# Revit family: НЕВАТОМ_Секция бактерицидная SUB_20220407
name_source: partatom
category: Арматура воздуховодов
revit_build: Autodesk Revit 2017 (Build: 20170118_1100(x64)
units: mm (PartAtom-declared; Revit-internal decimal feet)

## family parameters
Всегда вертикально = Нет
На основе рабочей плоскости = Нет
Общий = Нет
При загрузке вырезать с полостями = Нет
Размер круглого соединителя = Использовать диаметр
Тип детали = Вставляется

## types (48) — shared parameters
ADSK_Завод-изготовитель = NEVATOM
ADSK_Материал наименование = Оцинкованная сталь
ADSK_Наименование = Секции ультрафиолетовой бактерицидной обработки (SUB)
ADSK_Напряжение = 230 В
ADSK_Потеря давления воздуха = 0.0 Па
ADSK_Размер_Ширина = 1440 мм
ADSK_Ток = 0 А
L = 1440 мм
Nevatom_URL = https://t.me
t = 2 мм
Материал корпуса = Материал корпуса
Толщина крышки = 50 мм

## per-type parameters (varying)
| type | A | ADSK_Единица измерения | ADSK_Марка | ADSK_Масса | ADSK_Масса_Текст | ADSK_Полная мощность | ADSK_Размер_Высота | ADSK_Размер_Длина | ADSK_Расход воздуха | B | C | D | E | F | M |
| SUB-400х200-2 | 400 мм | шт. | 400х200-2 | 17 | 17.0 кг | 0 кВт | 250 мм | 450 мм | 1152.0 м³/ч | 200 мм | 450 мм | 250 мм | 423 мм | 223 мм | 9 мм |
| SUB-400х200-4 | 400 мм | шт. | 400х200-4 | 20 | 20.0 кг | 0 кВт | 250 мм | 450 мм | 1152.0 м³/ч | 200 мм | 450 мм | 250 мм | 423 мм | 223 мм | 9 мм |
| SUB-400х200-6 | 400 мм | шт. | 400х200-6 | 22 | 22.0 кг | 0 кВт | 250 мм | 450 мм | 1152.0 м³/ч | 200 мм | 450 мм | 250 мм | 423 мм | 223 мм | 9 мм |
| SUB-400х200-8 | 400 мм | шт. | 400х200-8 | 25 | 25.0 кг | 1 кВт | 250 мм | 450 мм | 1152.0 м³/ч | 200 мм | 450 мм | 250 мм | 423 мм | 223 мм | 9 мм |
| SUB-500х250-2 | 500 мм | шт. | 500х250-2 | 21 | 21.0 кг | 0 кВт | 300 мм | 550 мм | 1800.0 м³/ч | 250 мм | 550 мм | 300 мм | 523 мм | 273 мм | 9 мм |
| SUB-500х250-4 | 500 мм | шт. | 500х250-4 | 23 | 23.0 кг | 0 кВт | 300 мм | 550 мм | 1800.0 м³/ч | 250 мм | 550 мм | 300 мм | 523 мм | 273 мм | 9 мм |
| SUB-500х250-6 | 500 мм | шт. | 500х250-6 | 25 | 25.0 кг | 0 кВт | 300 мм | 550 мм | 1800.0 м³/ч | 250 мм | 550 мм | 300 мм | 523 мм | 273 мм | 9 мм |
| SUB-500х250-8 | 500 мм | шт. | 500х250-8 | 28 | 28.0 кг | 1 кВт | 300 мм | 550 мм | 1800.0 м³/ч | 250 мм | 550 мм | 300 мм | 523 мм | 273 мм | 9 мм |
| SUB-500х250-10 | 500 мм | шт. | 500х250-10 | 30 | 30.0 кг | 1 кВт | 300 мм | 550 мм | 1800.0 м³/ч | 250 мм | 550 мм | 300 мм | 523 мм | 273 мм | 9 мм |
| SUB-500х250-12 | 500 мм | шт. | 500х250-12 | 33 | 33.0 кг | 1 кВт | 300 мм | 550 мм | 1800.0 м³/ч | 250 мм | 550 мм | 300 мм | 523 мм | 273 мм | 9 мм |
| SUB-500х300-4 | 500 мм | шт. | 500х300-4 | 24 | 24.0 кг | 0 кВт | 350 мм | 550 мм | 2150.0 м³/ч | 300 мм | 550 мм | 350 мм | 523 мм | 323 мм | 9 мм |
| SUB-500х300-6 | 500 мм | шт. | 500х300-6 | 27 | 27.0 кг | 0 кВт | 350 мм | 550 мм | 2150.0 м³/ч | 300 мм | 550 мм | 350 мм | 523 мм | 323 мм | 9 мм |
| SUB-500х300-8 | 500 мм | шт. | 500х300-8 | 29 | 29.0 кг | 1 кВт | 350 мм | 550 мм | 2150.0 м³/ч | 300 мм | 550 мм | 350 мм | 523 мм | 323 мм | 9 мм |
| SUB-500х300-10 | 500 мм | шт. | 500х300-10 | 31 | 31.0 кг | 1 кВт | 350 мм | 550 мм | 2150.0 м³/ч | 300 мм | 550 мм | 350 мм | 523 мм | 323 мм | 9 мм |
| SUB-500х300-12 | 500 мм | шт. | 500х300-12 | 34 | 34.0 кг | 1 кВт | 350 мм | 550 мм | 2150.0 м³/ч | 300 мм | 550 мм | 350 мм | 523 мм | 323 мм | 9 мм |
| SUB-600х300-4 | 600 мм | шт. | 600х300-4 | 28 | 28.0 кг | 0 кВт | 350 мм | 650 мм | 2600.0 м³/ч | 300 мм | 650 мм | 350 мм | 623 мм | 323 мм | 9 мм |
| SUB-600х300-6 | 600 мм | шт. | 600х300-6 | 29 | 29.0 кг | 0 кВт | 350 мм | 650 мм | 2600.0 м³/ч | 300 мм | 650 мм | 350 мм | 623 мм | 323 мм | 9 мм |
| SUB-600х300-8 | 600 мм | шт. | 600х300-8 | 30 | 30.0 кг | 1 кВт | 350 мм | 650 мм | 2600.0 м³/ч | 300 мм | 650 мм | 350 мм | 623 мм | 323 мм | 9 мм |
| SUB-600х300-10 | 600 мм | шт. | 600х300-10 | 31 | 31.0 кг | 1 кВт | 350 мм | 650 мм | 2600.0 м³/ч | 300 мм | 650 мм | 350 мм | 623 мм | 323 мм | 9 мм |
| SUB-600х300-12 | 600 мм | шт. | 600х300-12 | 32 | 32.0 кг | 1 кВт | 350 мм | 650 мм | 2600.0 м³/ч | 300 мм | 650 мм | 350 мм | 623 мм | 323 мм | 9 мм |
| SUB-600х300-14 | 600 мм | шт. | 600х300-14 | 33 | 33.0 кг | 1 кВт | 350 мм | 650 мм | 2600.0 м³/ч | 300 мм | 650 мм | 350 мм | 623 мм | 323 мм | 9 мм |
| SUB-600х350-4 | 600 мм | шт. | 600х350-4 | 29 | 29.0 кг | 0 кВт | 400 мм | 650 мм | 3000.0 м³/ч | 350 мм | 650 мм | 400 мм | 623 мм | 373 мм | 9 мм |
| SUB-600х350-6 | 600 мм | 31.0 шт. | 600х350-6 | 31 | кг | 0 кВт | 400 мм | 650 мм | 3000.0 м³/ч | 350 мм | 650 мм | 400 мм | 623 мм | 373 мм | 9 мм |
| SUB-600х350-8 | 600 мм | шт. | 600х350-8 | 33 | 33.0 кг | 1 кВт | 400 мм | 650 мм | 3000.0 м³/ч | 350 мм | 650 мм | 400 мм | 623 мм | 373 мм | 9 мм |
| SUB-600х350-10 | 600 мм | шт. | 600х350-10 | 36 | 36.0 кг | 1 кВт | 400 мм | 650 мм | 3000.0 м³/ч | 350 мм | 650 мм | 400 мм | 623 мм | 373 мм | 9 мм |
| SUB-600х350-12 | 600 мм | шт. | 600х350-12 | 39 | 39.0 кг | 1 кВт | 400 мм | 650 мм | 3000.0 м³/ч | 350 мм | 650 мм | 400 мм | 623 мм | 373 мм | 9 мм |
| SUB-600х350-14 | 600 мм | шт. | 600х350-14 | 41 | 41.0 кг | 1 кВт | 400 мм | 650 мм | 3000.0 м³/ч | 350 мм | 650 мм | 400 мм | 623 мм | 373 мм | 9 мм |
| SUB-700х400-6 | 700 мм | шт. | 700х400-6 | 34 | 34.0 кг | 0 кВт | 457 мм | 757 мм | 4000.0 м³/ч | 400 мм | 757 мм | 457 мм | 727 мм | 427 мм | 11 мм |
| SUB-700х400-10 | 700 мм | шт. | 700х400-10 | 39 | 39.0 кг | 1 кВт | 457 мм | 757 мм | 4000.0 м³/ч | 400 мм | 757 мм | 457 мм | 727 мм | 427 мм | 11 мм |
| SUB-700х400-12 | 700 мм | шт. | 700х400-12 | 41 | 41.0 кг | 1 кВт | 457 мм | 757 мм | 4000.0 м³/ч | 400 мм | 757 мм | 457 мм | 727 мм | 427 мм | 11 мм |
| SUB-700х400-14 | 700 мм | шт. | 700х400-14 | 44 | 44.0 кг | 1 кВт | 457 мм | 757 мм | 4000.0 м³/ч | 400 мм | 757 мм | 457 мм | 727 мм | 427 мм | 11 мм |
| SUB-700х400-18 | 700 мм | шт. | 700х400-18 | 48 | 48.0 кг | 1 кВт | 457 мм | 757 мм | 4000.0 м³/ч | 400 мм | 757 мм | 457 мм | 727 мм | 427 мм | 11 мм |
| SUB-800х500-8 | 800 мм | шт. | 800х500-8 | 41 | 41.0 кг | 1 кВт | 557 мм | 857 мм | 5700.0 м³/ч | 500 мм | 857 мм | 557 мм | 827 мм | 527 мм | 11 мм |
| SUB-800х500-10 | 800 мм | шт. | 800х500-10 | 44 | 44.0 кг | 1 кВт | 557 мм | 857 мм | 5700.0 м³/ч | 500 мм | 857 мм | 557 мм | 827 мм | 527 мм | 11 мм |
| SUB-800х500-14 | 800 мм | шт. | 800х500-14 | 49 | 49.0 кг | 1 кВт | 557 мм | 857 мм | 5700.0 м³/ч | 500 мм | 857 мм | 557 мм | 827 мм | 527 мм | 11 мм |
| SUB-800х500-18 | 800 мм | шт. | 800х500-18 | 54 | 54.0 кг | 1 кВт | 557 мм | 857 мм | 5700.0 м³/ч | 500 мм | 857 мм | 557 мм | 827 мм | 527 мм | 11 мм |
| SUB-800х500-20 | 800 мм | шт. | 800х500-20 | 56 | 56.0 кг | 2 кВт | 557 мм | 857 мм | 5700.0 м³/ч | 500 мм | 857 мм | 557 мм | 827 мм | 527 мм | 11 мм |
| SUB-800х500-24 | 800 мм | шт. | 800х500-24 | 61 | 61.0 кг | 2 кВт | 557 мм | 857 мм | 5700.0 м³/ч | 500 мм | 857 мм | 557 мм | 827 мм | 527 мм | 11 мм |
| SUB-900х500-8 | 900 мм | шт. | 900х500-8 | 44 | 44.0 кг | 1 кВт | 557 мм | 957 мм | 6500.0 м³/ч | 500 мм | 957 мм | 557 мм | 927 мм | 527 мм | 11 мм |
| SUB-900х500-14 | 900 мм | шт. | 900х500-14 | 51 | 51.0 кг | 1 кВт | 557 мм | 957 мм | 6500.0 м³/ч | 500 мм | 957 мм | 557 мм | 927 мм | 527 мм | 11 мм |
| SUB-900х500-18 | 900 мм | шт. | 900х500-18 | 56 | 56.0 кг | 1 кВт | 557 мм | 957 мм | 6500.0 м³/ч | 500 мм | 957 мм | 557 мм | 927 мм | 527 мм | 11 мм |
| SUB-900х500-20 | 900 мм | шт. | 900х500-20 | 60 | 60.0 кг | 2 кВт | 557 мм | 957 мм | 6500.0 м³/ч | 500 мм | 957 мм | 557 мм | 927 мм | 527 мм | 11 мм |
| SUB-900х500-24 | 900 мм | шт. | 900х500-24 | 63 | 63.0 кг | 2 кВт | 557 мм | 957 мм | 6500.0 м³/ч | 500 мм | 957 мм | 557 мм | 927 мм | 527 мм | 11 мм |
| SUB-1000х500-10 | 1000 мм | шт. | 1000х500-10 | 48 | 48.0 кг | 1 кВт | 557 мм | 1057 мм | 7200.0 м³/ч | 500 мм | 1057 мм | 557 мм | 1027 мм | 527 мм | 11 мм |
| SUB-1000х500-14 | 1000 мм | шт. | 1000х500-14 | 53 | 53.0 кг | 1 кВт | 557 мм | 1057 мм | 7200.0 м³/ч | 500 мм | 1057 мм | 557 мм | 1027 мм | 527 мм | 11 мм |
| SUB-1000х500-18 | 1000 мм | шт. | 1000х500-18 | 58 | 58.0 кг | 1 кВт | 557 мм | 1057 мм | 7200.0 м³/ч | 500 мм | 1057 мм | 557 мм | 1027 мм | 527 мм | 11 мм |
| SUB-1000х500-20 | 1000 мм | шт. | 1000х500-20 | 60 | 60 кг | 2 кВт | 557 мм | 1057 мм | 7200.0 м³/ч | 500 мм | 1057 мм | 557 мм | 1027 мм | 527 мм | 11 мм |
| SUB-1000х500-24 | 1000 мм | шт. | 1000х500-24 | 65 | 65.0 кг | 2 кВт | 557 мм | 1057 мм | 7200.0 м³/ч | 500 мм | 1057 мм | 557 мм | 1027 мм | 527 мм | 11 мм |
